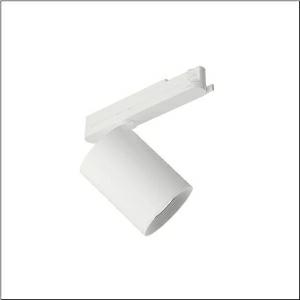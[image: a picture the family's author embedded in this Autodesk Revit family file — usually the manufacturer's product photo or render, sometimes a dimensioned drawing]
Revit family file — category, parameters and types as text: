
# Revit family: spot_21_51se12mbd5b
name_source: partatom
category: Lighting Fixtures
units: mm (PartAtom-declared; Revit-internal decimal feet)

## family parameters
Cut with Voids When Loaded = No
Host = Face
Light Source = No
Part Type = Normal
Room Calculation Point = No
Round Connector Dimension = Use Diameter
Shared = No

## types (1)
- --- (1 x LED, 5460 lm, 41.5 W, 4000K)
    Apparent Load = 42 VA
    CIE Flux Codes = 95 98 99 100 100
    Color Rendering = 90
    Color Temperature = 4000K
    Default Elevation = 1800 mm
    Description = Spot 21, directional spotlight, light control with lens, of PMMA, LED rated luminous flux: 5.250lm, light colour: 940, control gear: ECG Multilumen, with 3-phase adapter, mains connection: 220..240V, AC, 50/60Hz, of aluminium, traffic white (RAL 9016), length: 213mm, diameter: 105mm, protection rating (complete): IP20, insulation class (complete): insulation class I (protective earthing), certification: CE, impact resistance: IK02, permissible ambient temperature for indoor applications: -20..+40°C, packaging unit: 1 piece
    Height = 175 mm
    Lamp = 1 x LED
    Lamp Light Flux = 5460 lm
    Lamp Power = 41.5 W
    Lamp count = 1
    Length = 105 mm
    Luminous efficacy = 132 lm/W
    Manufacturer = Siteco
    ModVariant = No
    Model = 51SE12MBD5B
    Mounting Place = Ceiling
    Mounting Type = Pendant
    Number of Poles = 1
    OnlyDefault = Yes
    Power Factor = 1
    Product Name = Spot 21
    Product group = directional spotlight
    ProductGroupID = 904
    Protection Class = Protection class I
    Protection Degree = IP 20
    RLX_Detail_Level = 1
    RlxData = <blob elided: 17617 chars, md5=255ed418>
    Socket = socket
    Standby Power = 0 W
    System Light Flux = 5460 lm
    System Power = 42 W
    Type Comments = factory setting: luminous flux: 100 % | (ON | ON | ON | ON) | 1050 mA
    Type Image = l_1003976.jpg
    URL = http://relux.com
    VarID = @adj_053661
    Voltage = 0 V
    Weight = 0.00 kg
    Width = 0 mm  [stored 0 ft]

note: [stored X ft] marks values corroborated as IEEE doubles in the binary element streams (Revit-internal decimal feet)

## geometry (parser evidence)
native form markers: Blend x4, Sweep x10
no freeform markers — native parametric forms only
